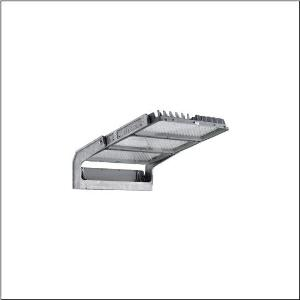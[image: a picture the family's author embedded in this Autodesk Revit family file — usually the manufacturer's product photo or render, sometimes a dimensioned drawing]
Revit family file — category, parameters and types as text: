
# Revit family: floodlight_fl_11_maxi_pro___rs07_5xa779229k01gb_e668
name_source: partatom
category: Lighting Fixtures
units: mm (PartAtom-declared; Revit-internal decimal feet)

## family parameters
Cut with Voids When Loaded = No
Host = Face
Light Source = No
Part Type = Normal
Room Calculation Point = No
Round Connector Dimension = Use Diameter
Shared = No

## types (1)
- --- (1 x LED, 164870 lm, 1315 W, 5700K)
    Apparent Load = 1315 VA
    CIE Flux Codes = 80 93 99 100 99
    Color Rendering = 70
    Color Temperature = 5700K
    Default Elevation = 1800 mm
    Description = Floodlight FL 11  maxi  pro floodlight; light control with lens of PMMA; cover panel of toughened safety glass, transparent; light distribution: RS07, rotationally symmetric direct distribution, LED; colour temperature: 5700K, rated luminous flux: 164.870lm, colour rendering: CRI > 70, light colour: 757; luminous efficacy: 125lm/W; brightness control: DMX+RDM; with terminal, 5-pole, max. 2.5mm², mains connection: 220..240V/380..400V AC, 50/60Hz, surge voltage resistance: line to ground: 10kV, LED service life up to 100,000h L90. Typical operating time: 1000h per year., ECG replaceable separately, LED unit replaceable without ESD environment, dustproof LED module, dimming range 10..100%; 1315W floodlight with 3x LED unit of diecast aluminium, coated grey; length: 1.003mm / width: 651mm / height: 338mm; mounting bracket, of diecast aluminium, uncoated, natural, equipment: Power, protection rating (complete): IP66; insulation class (complete): insulation class I (protective earthing); certification: CE, ENEC, VDE; ball protection: ball impact resistant, only for outdoor installations in the designated locations, permissible operating ambient temperature: -45..+55°C, permissible storage temperature: -40..+85°Cpackaging unit: 1 piece

Light Distribution: RS07
    Height = 320 mm
    Lamp = 1 x LED
    Lamp Light Flux = 164870 lm
    Lamp Power = 1315 W
    Lamp count = 1
    Length = 1002 mm
    Luminous efficacy = 125 lm/W
    Manufacturer = Siteco
    ModVariant = No
    Model = 5XA779229K01GB
    Mounting Place = Ceiling
    Mounting Type = Surface mounted
    Number of Poles = 1
    OnlyDefault = Yes
    Power Factor = 1
    Product Name = Floodlight FL 11 maxi pro | RS07
    Product group = floodlight | ceiling mounted
    ProductGroupID = 303
    Protection Class = Protection class I
    Protection Degree = IP 66
    RLX_Detail_Level = 1
    RLX_Emergency_Light_Flux = 0 lm
    RLX_Emergency_Type = 0
    RLX_Emergency_Type_DB = No
    RlxData = <blob elided: 40229 chars, md5=be028414>
    Socket = socket
    Standby Power = 0 W
    System Light Flux = 164870 lm
    System Power = 1315 W
    Type Comments = factory setting: luminous flux: 100 % | dim-lin: 255 | 895 mA
    Type Image = l_1356210.jpg
    URL = http://relux.com
    VarID = @adj_033341
    Voltage = 0 V
    Weight = 0.00 kg
    Width = 655 mm

## geometry (parser evidence)
native form markers: Blend x4, Sweep x13
no freeform markers — native parametric forms only
